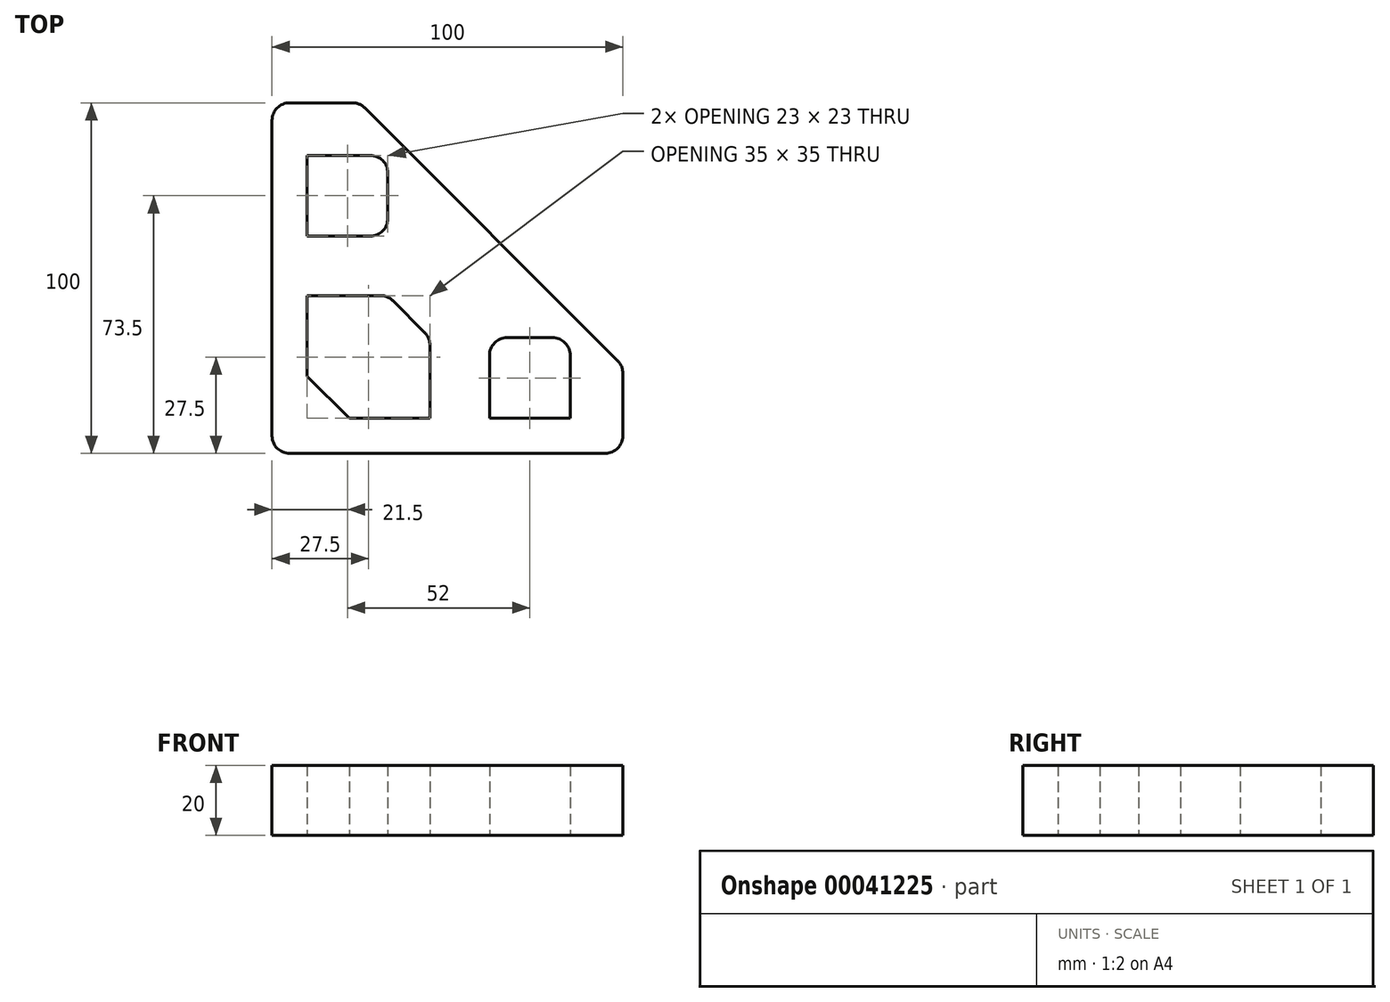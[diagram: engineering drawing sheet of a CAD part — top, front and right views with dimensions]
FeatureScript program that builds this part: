
annotation { "Feature Type Name" : "Feature", "Feature Type Description" : "" }
export const myFeature = defineFeature(function(context is Context, id is Id, definition is map)
    precondition{}
    {
        {
            var Q0;
            Q0=qCreatedBy(makeId("Top.planeOp"),FACE);
            var sketch = newSketch(context, id + "F0", { "sketchPlane" : qUnion([Q0])});
            skLineSegment(sketch, "E0", {"start": v(0, 0) * mm, "end": v(0, 100) * mm});
            skLineSegment(sketch, "E1", {"start": v(0, 0) * mm, "end": v(100, 0) * mm});
            skLineSegment(sketch, "E2", {"start": v(0, 100) * mm, "end": v(25, 100) * mm});
            skLineSegment(sketch, "E3", {"start": v(25, 100) * mm, "end": v(100, 25) * mm});
            skLineSegment(sketch, "E4", {"start": v(100, 25) * mm, "end": v(100, 0) * mm});
            skLineSegment(sketch, "E5.bottom", {"start": v(62, 33) * mm, "end": v(85, 33) * mm});
            skLineSegment(sketch, "E5.top", {"start": v(62, 10) * mm, "end": v(85, 10) * mm});
            skLineSegment(sketch, "E5.left", {"start": v(62, 33) * mm, "end": v(62, 10) * mm});
            skLineSegment(sketch, "E5.right", {"start": v(85, 33) * mm, "end": v(85, 10) * mm});
            skPoint(sketch, "E6", {"position": v(62.5, 62.5) * mm});
            skLineSegment(sketch, "E7", {"start": v(0, 0) * mm, "end": v(62.5, 62.5) * mm, "construction": true});
            skLineSegment(sketch, "E8.MirrorCS", {"start": v(33, 62) * mm, "end": v(10, 62) * mm});
            skLineSegment(sketch, "E9.MirrorCS", {"start": v(33, 62) * mm, "end": v(33, 85) * mm});
            skLineSegment(sketch, "E10.MirrorCS", {"start": v(33, 85) * mm, "end": v(10, 85) * mm});
            skLineSegment(sketch, "E11.MirrorCS", {"start": v(10, 62) * mm, "end": v(10, 85) * mm});
            skLineSegment(sketch, "E12.top", {"start": v(22, 10) * mm, "end": v(45, 10) * mm});
            skLineSegment(sketch, "E12.right", {"start": v(45, 33) * mm, "end": v(45, 10) * mm});
            skLineSegment(sketch, "E13.MirrorCS", {"start": v(33, 45) * mm, "end": v(10, 45) * mm});
            skLineSegment(sketch, "E14.MirrorCS", {"start": v(10, 22) * mm, "end": v(10, 45) * mm});
            skLineSegment(sketch, "E15", {"start": v(33, 45) * mm, "end": v(45, 33) * mm});
            skLineSegment(sketch, "E16", {"start": v(10, 22) * mm, "end": v(22, 10) * mm});
            skPoint(sketch, "E17.MirrorCS.start.orphan", {"position": v(30, 23.16) * mm});
            skPoint(sketch, "E12.bottom.start.orphan", {"position": v(23.16, 30) * mm});
            skPoint(sketch, "E18.orphan", {"position": v(10, 22) * mm});
            skSolve(sketch);
        }
        {
            var Q0;
            Q0=makeQuery(id+"F0.imprint","IMPRINT",FACE,{"disambiguationData":[TD([[makeQuery(id+"F0.imprint","IMPRINT",EDGE,{"derivedFrom":sQuery(id+"F0.wireOp",EDGE,"E0")}),-1.0]])]});
            extrude(context, id + "F1", {"entities" : qUnion([Q0]), "depth" : 20 * mm});
        }
        {
            var Q0;
            Q0=makeQuery(id+"F1.opExtrude","SWEPT_EDGE",EDGE,{"disambiguationData":[OSD([sQuery(id+"F0.wireOp",EDGE,"E0"),sQuery(id+"F0.wireOp",EDGE,"E2")])]});
            var Q1;
            Q1=makeQuery(id+"F1.opExtrude","SWEPT_EDGE",EDGE,{"disambiguationData":[OSD([sQuery(id+"F0.wireOp",EDGE,"E2"),sQuery(id+"F0.wireOp",EDGE,"E3")])]});
            var Q2;
            Q2=makeQuery(id+"F1.opExtrude","SWEPT_EDGE",EDGE,{"disambiguationData":[OSD([sQuery(id+"F0.wireOp",EDGE,"E3"),sQuery(id+"F0.wireOp",EDGE,"E4")])]});
            var Q3;
            Q3=makeQuery(id+"F1.opExtrude","SWEPT_EDGE",EDGE,{"disambiguationData":[OSD([sQuery(id+"F0.wireOp",EDGE,"E1"),sQuery(id+"F0.wireOp",EDGE,"E4")])]});
            var Q4;
            Q4=makeQuery(id+"F1.opExtrude","SWEPT_EDGE",EDGE,{"disambiguationData":[OSD([sQuery(id+"F0.wireOp",EDGE,"E13.MirrorCS"),sQuery(id+"F0.wireOp",EDGE,"E15")])]});
            var Q5;
            Q5=makeQuery(id+"F1.opExtrude","SWEPT_EDGE",EDGE,{"disambiguationData":[OSD([sQuery(id+"F0.wireOp",EDGE,"E12.right"),sQuery(id+"F0.wireOp",EDGE,"E15")])]});
            var Q6;
            Q6=makeQuery(id+"F1.opExtrude","SWEPT_EDGE",EDGE,{"disambiguationData":[OSD([sQuery(id+"F0.wireOp",EDGE,"E5.bottom"),sQuery(id+"F0.wireOp",EDGE,"E5.right")])]});
            var Q7;
            Q7=makeQuery(id+"F1.opExtrude","SWEPT_EDGE",EDGE,{"disambiguationData":[OSD([sQuery(id+"F0.wireOp",EDGE,"E9.MirrorCS"),sQuery(id+"F0.wireOp",EDGE,"E10.MirrorCS")])]});
            var Q8;
            Q8=makeQuery(id+"F1.opExtrude","SWEPT_EDGE",EDGE,{"disambiguationData":[OSD([sQuery(id+"F0.wireOp",EDGE,"E5.bottom"),sQuery(id+"F0.wireOp",EDGE,"E5.left")])]});
            var Q9;
            Q9=makeQuery(id+"F1.opExtrude","SWEPT_EDGE",EDGE,{"disambiguationData":[OSD([sQuery(id+"F0.wireOp",EDGE,"E8.MirrorCS"),sQuery(id+"F0.wireOp",EDGE,"E9.MirrorCS")])]});
            var Q10;
            Q10=makeQuery(id+"F1.opExtrude","SWEPT_EDGE",EDGE,{"disambiguationData":[OSD([sQuery(id+"F0.wireOp",EDGE,"E0"),sQuery(id+"F0.wireOp",EDGE,"E1")])]});
            fillet(context, id + "F2", {"entities" : qUnion([Q0, Q1, Q2, Q3, Q4, Q5, Q6, Q7, Q8, Q9, Q10]), "radius" : 5 * mm, "tangentPropagation" : true, "allowEdgeOverflow" : false});
        }
    });
